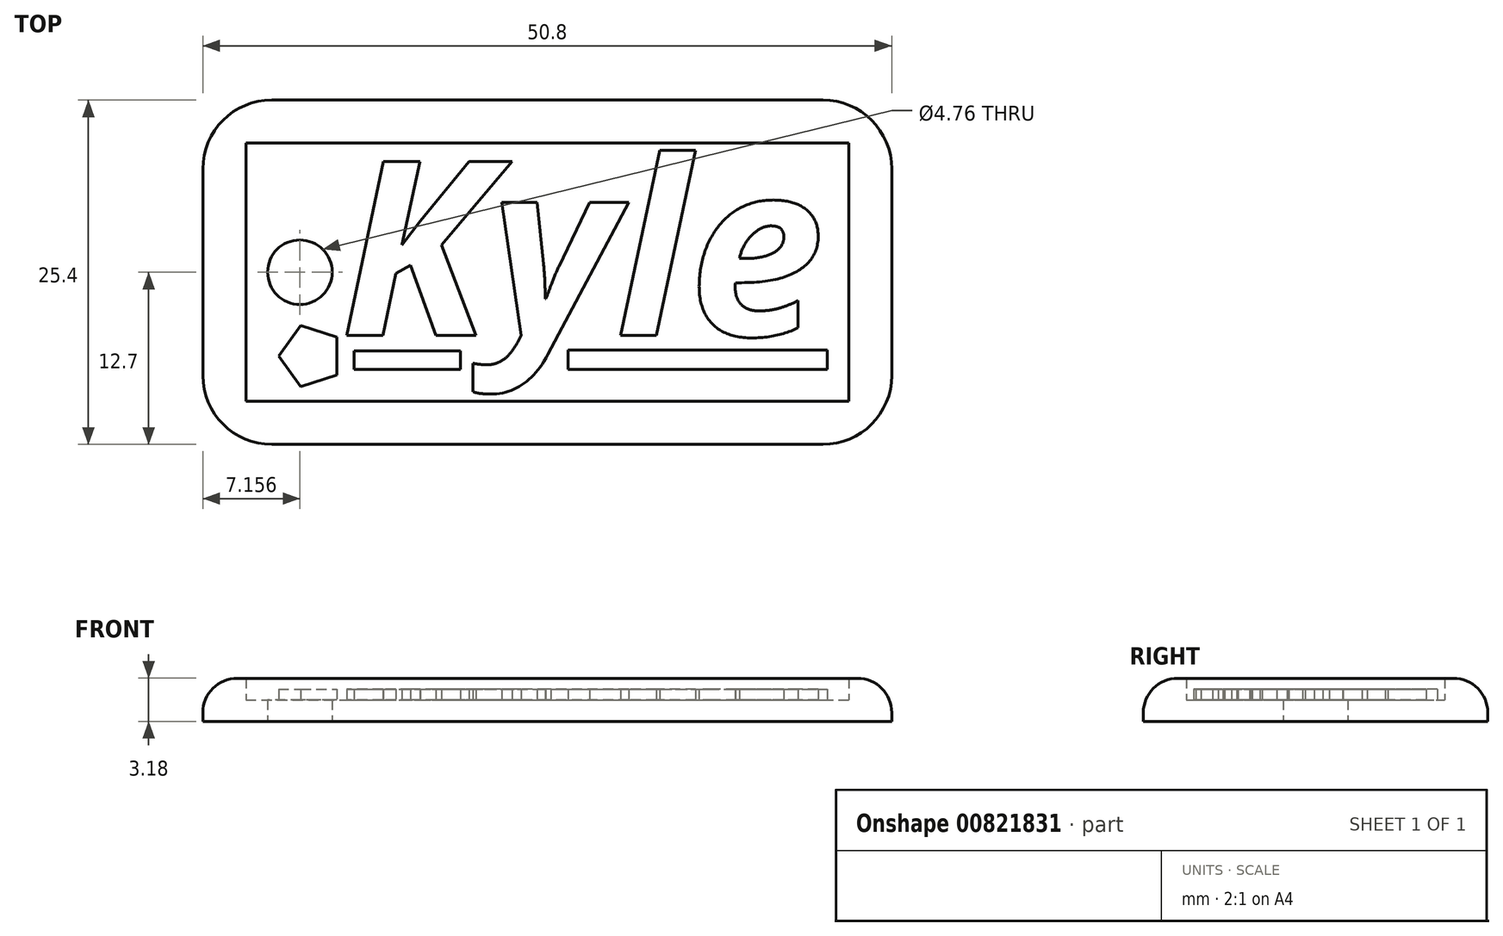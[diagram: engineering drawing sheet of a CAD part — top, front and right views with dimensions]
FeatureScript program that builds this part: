
annotation { "Feature Type Name" : "Feature", "Feature Type Description" : "" }
export const myFeature = defineFeature(function(context is Context, id is Id, definition is map)
    precondition{}
    {
        {
            var Q0;
            Q0=qCreatedBy(makeId("Top.planeOp"),FACE);
            var sketch = newSketch(context, id + "F0", { "sketchPlane" : qUnion([Q0])});
            skLineSegment(sketch, "E0.bottom", {"start": v(0, 0) * mm, "end": v(50.8, 0) * mm});
            skLineSegment(sketch, "E0.top", {"start": v(0, 25.4) * mm, "end": v(50.8, 25.4) * mm});
            skLineSegment(sketch, "E0.left", {"start": v(0, 0) * mm, "end": v(0, 25.4) * mm});
            skLineSegment(sketch, "E0.right", {"start": v(50.8, 0) * mm, "end": v(50.8, 25.4) * mm});
            skCircle(sketch, "E1", {"center": v(7.16, 12.7) * mm, "radius": 2.38 * mm});
            skPoint(sketch, "E1.centerSnap0", {"position": v(0, 12.7) * mm});
            skLineSegment(sketch, "E2.0", {"start": v(3.18, 22.23) * mm, "end": v(47.62, 22.23) * mm});
            skLineSegment(sketch, "E2.1", {"start": v(3.18, 3.18) * mm, "end": v(3.18, 22.22) * mm});
            skLineSegment(sketch, "E2.2", {"start": v(3.18, 3.18) * mm, "end": v(47.62, 3.18) * mm});
            skLineSegment(sketch, "E2.3", {"start": v(47.62, 3.18) * mm, "end": v(47.62, 22.23) * mm});
            skSolve(sketch);
        }
        {
            var Q0;
            Q0=makeQuery(id+"F0.imprint","IMPRINT",FACE,{"disambiguationData":[TD([[makeQuery(id+"F0.imprint","IMPRINT",EDGE,{"derivedFrom":sQuery(id+"F0.wireOp",EDGE,"E1")}),-1.0]])]});
            extrude(context, id + "F1", {"entities" : qUnion([Q0]), "depth" : 1.59 * mm, "offsetDistance" : 25.4 * mm});
        }
        {
            var Q0;
            Q0 = qSketchRegion(id + "F0", true);
            extrude(context, id + "F2", {"entities" : qUnion([Q0]), "operationType" : NewBodyOperationType.ADD, "depth" : 3.17 * mm, "offsetDistance" : 25.4 * mm});
        }
        {
            var Q0;
            Q0=makeQuery(id+"F2.opExtrude","SWEPT_EDGE",EDGE,{"disambiguationData":[OSD([sQuery(id+"F0.wireOp",EDGE,"E0.bottom"),sQuery(id+"F0.wireOp",EDGE,"E0.right")])]});
            var Q1;
            Q1=makeQuery(id+"F2.opExtrude","SWEPT_EDGE",EDGE,{"disambiguationData":[OSD([sQuery(id+"F0.wireOp",EDGE,"E0.top"),sQuery(id+"F0.wireOp",EDGE,"E0.right")])]});
            var Q2;
            Q2=makeQuery(id+"F2.opExtrude","SWEPT_EDGE",EDGE,{"disambiguationData":[OSD([sQuery(id+"F0.wireOp",EDGE,"E0.top"),sQuery(id+"F0.wireOp",EDGE,"E0.left")])]});
            var Q3;
            Q3=makeQuery(id+"F2.opExtrude","SWEPT_EDGE",EDGE,{"disambiguationData":[OSD([sQuery(id+"F0.wireOp",EDGE,"E0.bottom"),sQuery(id+"F0.wireOp",EDGE,"E0.left")])]});
            fillet(context, id + "F3", {"entities" : qUnion([Q0, Q1, Q2, Q3]), "radius" : 5.08 * mm, "tangentPropagation" : true, "allowEdgeOverflow" : false});
        }
        {
            var Q0;
            Q0=makeQuery(id+"F2.opExtrude","CAP_EDGE",EDGE,{"disambiguationData":[OSD([sQuery(id+"F0.wireOp",EDGE,"E0.top")])],"isStart":false});
            fillet(context, id + "F4", {"entities" : qUnion([Q0]), "radius" : 2.54 * mm, "tangentPropagation" : true, "allowEdgeOverflow" : false});
        }
        {
            var Q0;
            Q0=makeQuery(id+"F1.opExtrude","CAP_FACE",FACE,{"disambiguationData":[OSD([sQuery(id+"F0.wireOp",EDGE,"E1"),sQuery(id+"F0.wireOp",EDGE,"E2.0"),sQuery(id+"F0.wireOp",EDGE,"E2.1"),sQuery(id+"F0.wireOp",EDGE,"E2.2"),sQuery(id+"F0.wireOp",EDGE,"E2.3")])],"isStart":false});
            var sketch = newSketch(context, id + "F5", { "sketchPlane" : qUnion([Q0])});
            skText(sketch, "E3", { "text": "Kyle", "fontName": "OpenSans-BoldItalic.ttf"});
            skCircle(sketch, "E4.cCircle", {"center": v(7.95, 6.5) * mm, "radius": 1.92 * mm, "construction": true});
            skLineSegment(sketch, "E4.0", {"start": v(9.87, 7.9) * mm, "end": v(9.87, 5.11) * mm});
            skLineSegment(sketch, "E4.1", {"start": v(9.87, 5.11) * mm, "end": v(7.22, 4.25) * mm});
            skLineSegment(sketch, "E4.2", {"start": v(7.22, 4.25) * mm, "end": v(5.58, 6.5) * mm});
            skLineSegment(sketch, "E4.3", {"start": v(5.58, 6.5) * mm, "end": v(7.22, 8.76) * mm});
            skLineSegment(sketch, "E4.4", {"start": v(7.22, 8.76) * mm, "end": v(9.87, 7.9) * mm});
            skPoint(sketch, "E4.0.midPoint", {"position": v(9.87, 6.5) * mm});
            skLineSegment(sketch, "E5.bottom", {"start": v(11.16, 6.9) * mm, "end": v(19, 6.9) * mm});
            skLineSegment(sketch, "E5.top", {"start": v(11.16, 5.52) * mm, "end": v(19, 5.52) * mm});
            skLineSegment(sketch, "E5.left", {"start": v(11.16, 6.9) * mm, "end": v(11.16, 5.52) * mm});
            skLineSegment(sketch, "E5.right", {"start": v(19, 6.9) * mm, "end": v(19, 5.52) * mm});
            skLineSegment(sketch, "E6.bottom", {"start": v(26.92, 6.97) * mm, "end": v(46.05, 6.97) * mm});
            skLineSegment(sketch, "E6.top", {"start": v(26.92, 5.52) * mm, "end": v(46.05, 5.52) * mm});
            skLineSegment(sketch, "E6.left", {"start": v(26.92, 6.97) * mm, "end": v(26.92, 5.52) * mm});
            skLineSegment(sketch, "E6.right", {"start": v(46.05, 6.97) * mm, "end": v(46.05, 5.52) * mm});
            const initialGuessF5  = {"E3": [0.01013, 0.00803, 1, 0, 0.01294]};
            skSetInitialGuess(sketch, initialGuessF5);
            skSolve(sketch);
        }
        {
            var Q0;
            Q0 = qSketchRegion(id + "F5", true);
            extrude(context, id + "F6", {"entities" : qUnion([Q0]), "operationType" : NewBodyOperationType.ADD, "depth" : 0.8 * mm, "offsetDistance" : 25.4 * mm});
        }
        {
            var Q0;
            Q0 = qSketchRegion(id + "F5", true);
            extrude(context, id + "F7", {"entities" : qUnion([Q0]), "operationType" : NewBodyOperationType.ADD, "depth" : 0.8 * mm, "offsetDistance" : 25.4 * mm});
        }
        {
            var Q0;
            Q0 = qSketchRegion(id + "F5", true);
            extrude(context, id + "F8", {"entities" : qUnion([Q0]), "operationType" : NewBodyOperationType.ADD, "depth" : 0.8 * mm, "offsetDistance" : 25.4 * mm});
        }
    });
